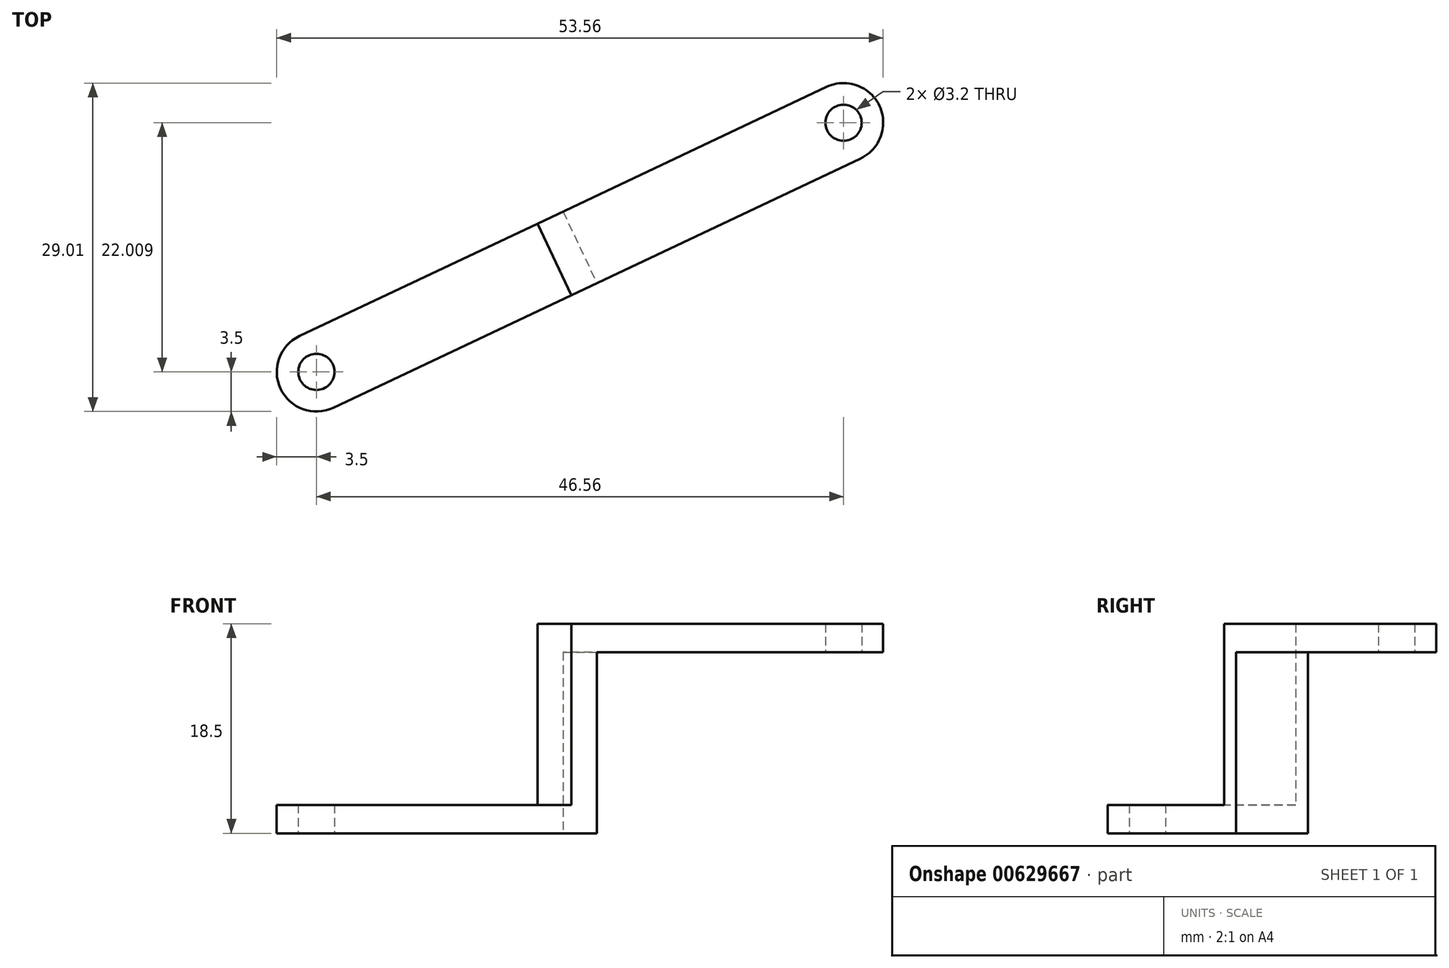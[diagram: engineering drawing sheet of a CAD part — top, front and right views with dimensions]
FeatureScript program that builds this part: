
annotation { "Feature Type Name" : "Feature", "Feature Type Description" : "" }
export const myFeature = defineFeature(function(context is Context, id is Id, definition is map)
    precondition{}
    {
        {
            var Q0;
            Q0=qCreatedBy(makeId("Top.planeOp"),FACE);
            cPlane(context, id + "F0", {"entities" : qUnion([Q0]), "cplaneType" : CPlaneType.OFFSET, "offset" : 16 * mm, "width" : 150 * mm, "height" : 150 * mm});
        }
        {
            var Q0;
            Q0=qCreatedBy(id+"F0.planeOp",FACE);
            var sketch = newSketch(context, id + "F1", { "sketchPlane" : qUnion([Q0])});
            skLineSegment(sketch, "E0", {"start": v(0, 0) * mm, "end": v(46.56, 22) * mm, "construction": true});
            skCircle(sketch, "E1", {"center": v(46.56, 22) * mm, "radius": 1.6 * mm});
            skCircle(sketch, "E2", {"center": v(46.56, 22) * mm, "radius": 3.5 * mm});
            skLineSegment(sketch, "E3", {"start": v(45.06, 25.17) * mm, "end": v(21.78, 14.17) * mm});
            skLineSegment(sketch, "E4.MirrorCS", {"start": v(48.06, 18.84) * mm, "end": v(24.78, 7.84) * mm});
            skLineSegment(sketch, "E5", {"start": v(21.78, 14.17) * mm, "end": v(24.78, 7.84) * mm});
            skSolve(sketch);
        }
        {
            var Q0;
            Q0=qSketchRegion(id+"F1",true);
            extrude(context, id + "F2", {"entities" : qUnion([Q0]), "depth" : 2.5 * mm});
        }
        {
            var Q0;
            Q0=makeQuery(id+"F2.opExtrude","SWEPT_FACE",FACE,{"disambiguationData":[OSD([sQuery(id+"F1.wireOp",EDGE,"E5")])]});
            var sketch = newSketch(context, id + "F3", { "sketchPlane" : qUnion([Q0])});
            skLineSegment(sketch, "E6.bottom", {"start": v(-3.5, 18.5) * mm, "end": v(3.5, 18.5) * mm});
            skLineSegment(sketch, "E6.top", {"start": v(-3.5, 0) * mm, "end": v(3.5, 0) * mm});
            skLineSegment(sketch, "E6.left", {"start": v(-3.5, 18.5) * mm, "end": v(-3.5, 0) * mm});
            skLineSegment(sketch, "E6.right", {"start": v(3.5, 18.5) * mm, "end": v(3.5, 0) * mm});
            skSolve(sketch);
        }
        {
            var Q0;
            Q0=qSketchRegion(id+"F3",true);
            extrude(context, id + "F4", {"entities" : qUnion([Q0]), "operationType" : NewBodyOperationType.ADD, "depth" : 2.5 * mm});
        }
        {
            var Q0;
            Q0=qCreatedBy(makeId("Top.planeOp"),FACE);
            var sketch = newSketch(context, id + "F5", { "sketchPlane" : qUnion([Q0])});
            skCircle(sketch, "E7", {"center": v(0, 0) * mm, "radius": 1.6 * mm});
            skCircle(sketch, "E8", {"center": v(0, 0) * mm, "radius": 3.5 * mm});
            skLineSegment(sketch, "E9", {"start": v(0, 0) * mm, "end": v(22.82, 10.79) * mm, "construction": true});
            skLineSegment(sketch, "E10", {"start": v(-1.5, 3.16) * mm, "end": v(19.52, 13.1) * mm});
            skLineSegment(sketch, "E11.MirrorCS", {"start": v(1.5, -3.16) * mm, "end": v(22.52, 6.77) * mm});
            skLineSegment(sketch, "E12.0", {"start": v(19.52, 13.1) * mm, "end": v(22.52, 6.77) * mm});
            skSolve(sketch);
        }
        {
            var Q0;
            Q0=qSketchRegion(id+"F5",true);
            extrude(context, id + "F6", {"entities" : qUnion([Q0]), "operationType" : NewBodyOperationType.ADD, "depth" : 2.5 * mm});
        }
    });
